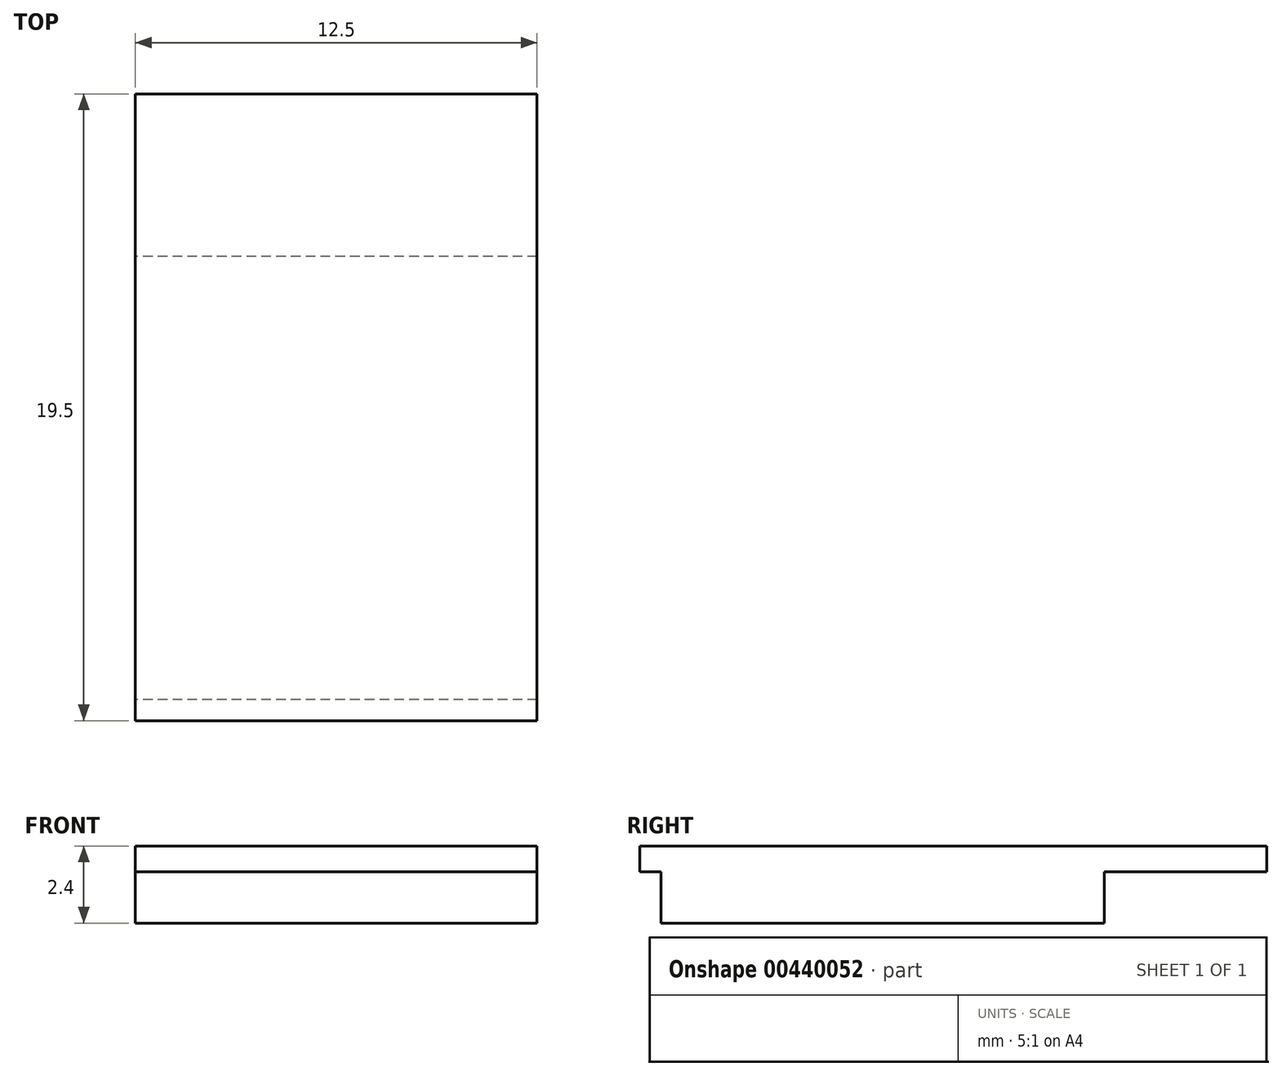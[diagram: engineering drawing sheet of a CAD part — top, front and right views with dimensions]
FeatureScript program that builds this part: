
annotation { "Feature Type Name" : "Feature", "Feature Type Description" : "" }
export const myFeature = defineFeature(function(context is Context, id is Id, definition is map)
    precondition{}
    {
        {
            var Q0;
            Q0=qCreatedBy(makeId("Top.planeOp"),FACE);
            var sketch = newSketch(context, id + "F0", { "sketchPlane" : qUnion([Q0])});
            skLineSegment(sketch, "E0.bottom", {"start": v(0, 0) * mm, "end": v(12.5, 0) * mm});
            skLineSegment(sketch, "E0.top", {"start": v(0, 19.5) * mm, "end": v(12.5, 19.5) * mm});
            skLineSegment(sketch, "E0.left", {"start": v(0, 0) * mm, "end": v(0, 19.5) * mm});
            skLineSegment(sketch, "E0.right", {"start": v(12.5, 0) * mm, "end": v(12.5, 19.5) * mm});
            skSolve(sketch);
        }
        {
            var Q0;
            Q0=makeQuery(id+"F0.imprint","IMPRINT",FACE,{"disambiguationData":[TD([[makeQuery(id+"F0.imprint","IMPRINT",EDGE,{"derivedFrom":sQuery(id+"F0.wireOp",EDGE,"E0.bottom")}),1.0]])]});
            var sketch = newSketch(context, id + "F1", { "sketchPlane" : qUnion([Q0])});
            skLineSegment(sketch, "E1", {"start": v(0, 0) * mm, "end": v(0, 0.65) * mm, "construction": true});
            skLineSegment(sketch, "E2", {"start": v(0, 0.65) * mm, "end": v(12.5, 0.65) * mm, "construction": true});
            skLineSegment(sketch, "E3", {"start": v(12.5, 0.65) * mm, "end": v(12.5, 14.45) * mm, "construction": true});
            skLineSegment(sketch, "E4.bottom", {"start": v(12.5, 14.45) * mm, "end": v(0, 14.45) * mm});
            skLineSegment(sketch, "E4.top", {"start": v(12.5, 0.65) * mm, "end": v(0, 0.65) * mm});
            skLineSegment(sketch, "E4.left", {"start": v(12.5, 14.45) * mm, "end": v(12.5, 0.65) * mm});
            skLineSegment(sketch, "E4.right", {"start": v(0, 14.45) * mm, "end": v(0, 0.65) * mm});
            skSolve(sketch);
        }
        {
            var Q0;
            Q0=makeQuery(id+"F0.imprint","IMPRINT",FACE,{"disambiguationData":[TD([[makeQuery(id+"F0.imprint","IMPRINT",EDGE,{"derivedFrom":sQuery(id+"F0.wireOp",EDGE,"E0.bottom")}),1.0]])]});
            extrude(context, id + "F2", {"entities" : qUnion([Q0]), "depth" : .8 * mm});
        }
        {
            var Q0;
            Q0 = qSketchRegion(id + "F1", true);
            extrude(context, id + "F3", {"entities" : qUnion([Q0]), "operationType" : NewBodyOperationType.ADD, "oppositeDirection" : true, "depth" : 1.6 * mm});
        }
    });
